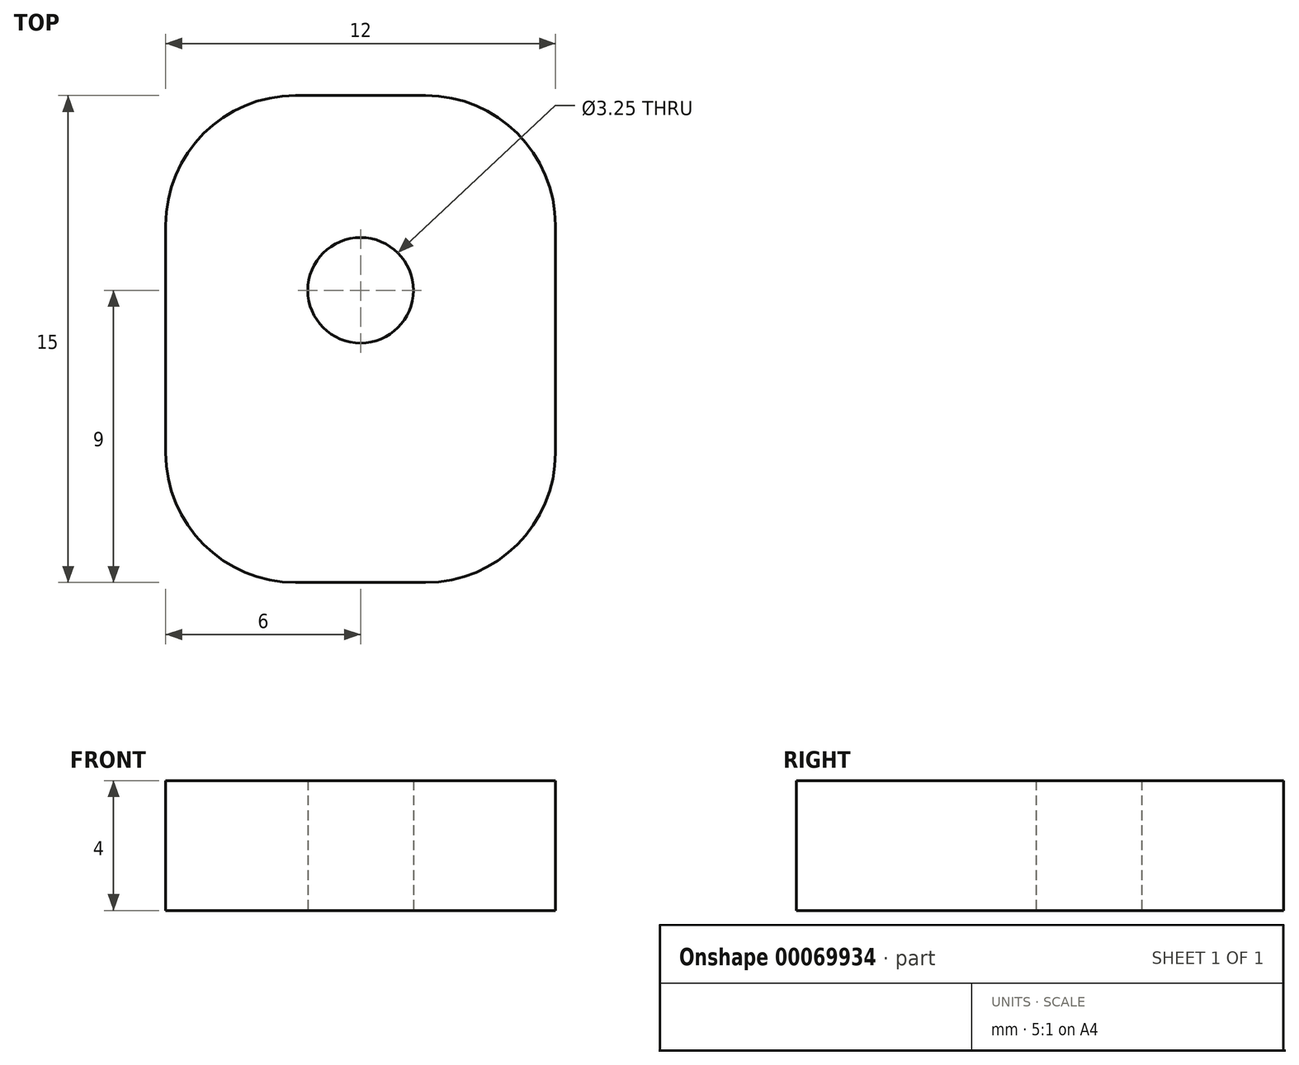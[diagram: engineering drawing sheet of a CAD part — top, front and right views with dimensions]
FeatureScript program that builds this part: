
annotation { "Feature Type Name" : "Feature", "Feature Type Description" : "" }
export const myFeature = defineFeature(function(context is Context, id is Id, definition is map)
    precondition{}
    {
        {
            var Q0;
            Q0=qCreatedBy(makeId("Top.planeOp"),FACE);
            var sketch = newSketch(context, id + "F0", { "sketchPlane" : qUnion([Q0])});
            skCircle(sketch, "E0", {"center": v(0, 0) * mm, "radius": 1.63 * mm});
            skLineSegment(sketch, "E1.rect.bottom", {"start": v(6, -6) * mm, "end": v(-6, -6) * mm, "construction": true});
            skLineSegment(sketch, "E1.rect.top", {"start": v(6, 6) * mm, "end": v(-6, 6) * mm});
            skLineSegment(sketch, "E1.rect.left", {"start": v(6, -6) * mm, "end": v(6, 6) * mm});
            skLineSegment(sketch, "E1.rect.right", {"start": v(-6, -6) * mm, "end": v(-6, 6) * mm});
            skLineSegment(sketch, "E2.rect.top", {"start": v(6, -9) * mm, "end": v(-6, -9) * mm});
            skLineSegment(sketch, "E2.rect.left", {"start": v(6, -6) * mm, "end": v(6, -9) * mm});
            skLineSegment(sketch, "E2.rect.right", {"start": v(-6, -6) * mm, "end": v(-6, -9) * mm});
            skPoint(sketch, "E2.rect.middle", {"position": v(0, -7.5) * mm});
            skSolve(sketch);
        }
        {
            var Q0;
            Q0=makeQuery(id+"F0.imprint","IMPRINT",FACE,{"disambiguationData":[TD([[makeQuery(id+"F0.imprint","IMPRINT",EDGE,{"derivedFrom":sQuery(id+"F0.wireOp",EDGE,"E0")}),-1.0]])]});
            extrude(context, id + "F1", {"entities" : qUnion([Q0]), "depth" : 4 * mm});
        }
        {
            var Q0;
            Q0=makeQuery(id+"F1.opExtrude","SWEPT_EDGE",EDGE,{"disambiguationData":[OSD([sQuery(id+"F0.wireOp",EDGE,"E1.rect.top"),sQuery(id+"F0.wireOp",EDGE,"E1.rect.right")])]});
            var Q1;
            Q1=makeQuery(id+"F1.opExtrude","SWEPT_EDGE",EDGE,{"disambiguationData":[OSD([sQuery(id+"F0.wireOp",EDGE,"E2.rect.top"),sQuery(id+"F0.wireOp",EDGE,"E2.rect.right")])]});
            var Q2;
            Q2=makeQuery(id+"F1.opExtrude","SWEPT_EDGE",EDGE,{"disambiguationData":[OSD([sQuery(id+"F0.wireOp",EDGE,"E2.rect.top"),sQuery(id+"F0.wireOp",EDGE,"E2.rect.left")])]});
            var Q3;
            Q3=makeQuery(id+"F1.opExtrude","SWEPT_EDGE",EDGE,{"disambiguationData":[OSD([sQuery(id+"F0.wireOp",EDGE,"E1.rect.top"),sQuery(id+"F0.wireOp",EDGE,"E1.rect.left")])]});
            fillet(context, id + "F2", {"entities" : qUnion([Q0, Q1, Q2, Q3]), "radius" : 4 * mm, "tangentPropagation" : true, "allowEdgeOverflow" : false});
        }
    });
